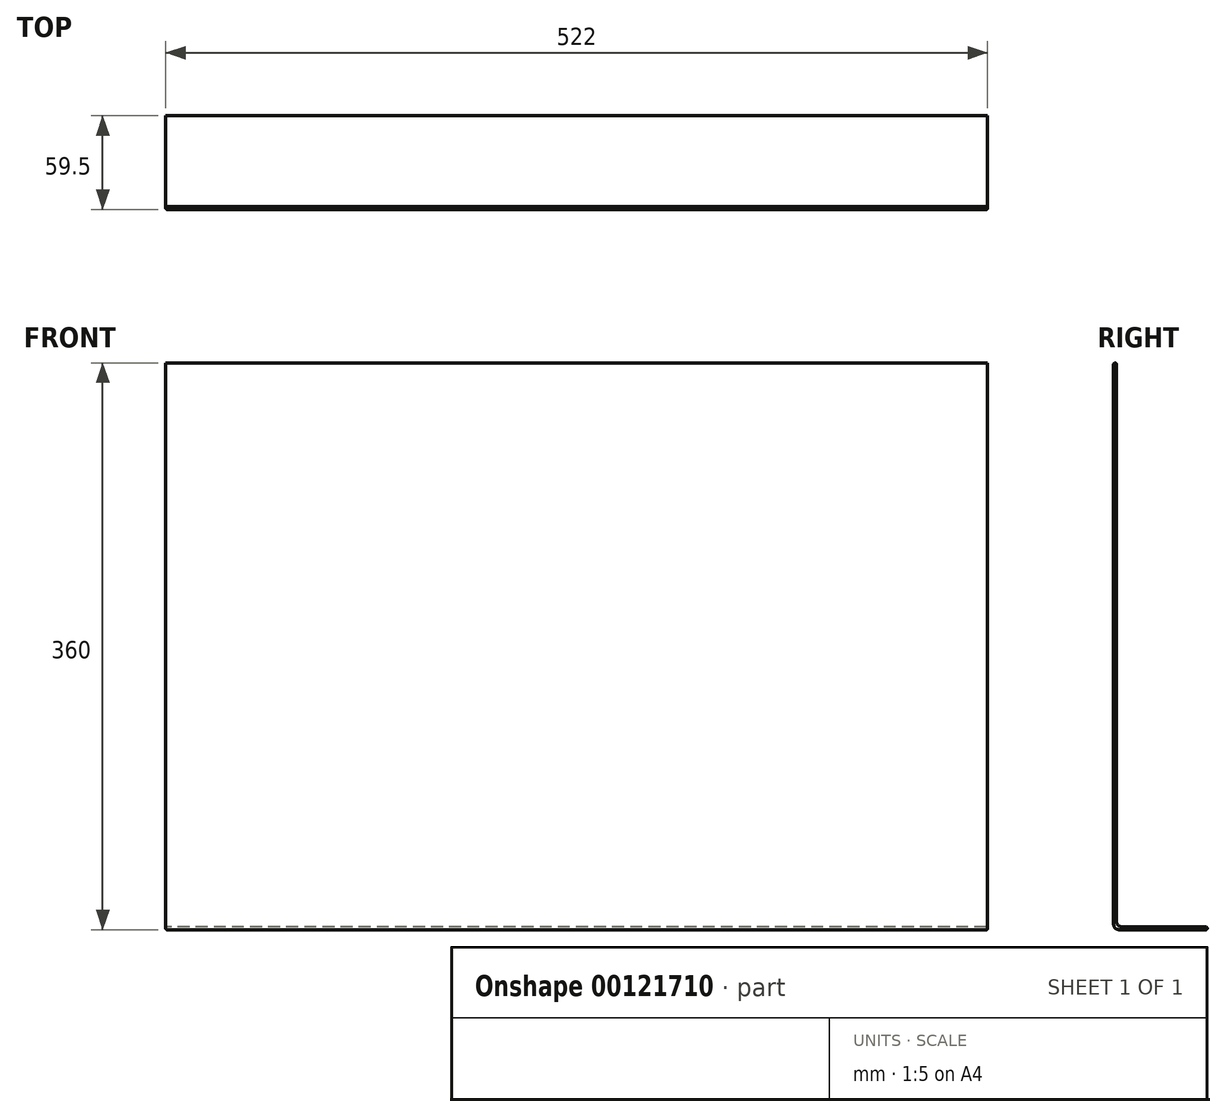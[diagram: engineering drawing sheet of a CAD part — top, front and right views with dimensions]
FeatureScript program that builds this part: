
annotation { "Feature Type Name" : "Feature", "Feature Type Description" : "" }
export const myFeature = defineFeature(function(context is Context, id is Id, definition is map)
    precondition{}
    {
        {
            assignVariable(context, id + "F0", {"name" : "thick", "anyValue" : 1.8});
        }
        {
            var Q0;
            Q0=qCreatedBy(makeId("Right.planeOp"),FACE);
            var sketch = newSketch(context, id + "F1", { "sketchPlane" : qUnion([Q0])});
            skLineSegment(sketch, "E0", {"start": v(0, 0) * mm, "end": v(0, 360) * mm});
            skLineSegment(sketch, "E1", {"start": v(0, 360) * mm, "end": v(1.8, 360) * mm});
            skLineSegment(sketch, "E2", {"start": v(1.8, 360) * mm, "end": v(1.8, 1.8) * mm});
            skLineSegment(sketch, "E3", {"start": v(1.8, 1.8) * mm, "end": v(59.5, 1.8) * mm});
            skLineSegment(sketch, "E4", {"start": v(59.5, 1.8) * mm, "end": v(59.5, 0) * mm});
            skLineSegment(sketch, "E5", {"start": v(59.5, 0) * mm, "end": v(0, 0) * mm});
            skSolve(sketch);
        }
        {
            var Q0;
            Q0=makeQuery(id+"F1.imprint","IMPRINT",FACE,{"disambiguationData":[TD([[makeQuery(id+"F1.imprint","IMPRINT",EDGE,{"derivedFrom":sQuery(id+"F1.wireOp",EDGE,"E0")}),-1.0]])]});
            extrude(context, id + "F2", {"entities" : qUnion([Q0]), "depth" : (522 / 2) * mm});
        }
        {
            var Q0;
            Q0=makeQuery(id+"F2.opExtrude","SWEPT_EDGE",EDGE,{"disambiguationData":[OSD([sQuery(id+"F1.wireOp",EDGE,"E2"),sQuery(id+"F1.wireOp",EDGE,"E3")])]});
            var Q1;
            Q1=makeQuery(id+"F2.opExtrude","SWEPT_EDGE",EDGE,{"disambiguationData":[OSD([sQuery(id+"F1.wireOp",EDGE,"E0"),sQuery(id+"F1.wireOp",EDGE,"E5")])]});
            fillet(context, id + "F3", {"entities" : qUnion([Q0, Q1]), "radius" : 2 * (getVariable(context, 'thick')) * mm, "tangentPropagation" : true, "allowEdgeOverflow" : false});
        }
        {
            var Q0;
            Q0=makeQuery(id+"F2.opExtrude","CAP_EDGE",EDGE,{"disambiguationData":[OSD([sQuery(id+"F1.wireOp",EDGE,"E3")])],"isStart":false});
            var Q1;
            Q1=makeQuery(id+"F2.opExtrude","CAP_EDGE",EDGE,{"disambiguationData":[OSD([sQuery(id+"F1.wireOp",EDGE,"E5")])],"isStart":false});
            var Q2;
            Q2=makeQuery(id+"F2.opExtrude","SWEPT_EDGE",EDGE,{"disambiguationData":[OSD([sQuery(id+"F1.wireOp",EDGE,"E3"),sQuery(id+"F1.wireOp",EDGE,"E4")])]});
            var Q3;
            Q3=makeQuery(id+"F2.opExtrude","SWEPT_EDGE",EDGE,{"disambiguationData":[OSD([sQuery(id+"F1.wireOp",EDGE,"E4"),sQuery(id+"F1.wireOp",EDGE,"E5")])]});
            var Q4;
            Q4=makeQuery(id+"F2.opExtrude","CAP_EDGE",EDGE,{"disambiguationData":[OSD([sQuery(id+"F1.wireOp",EDGE,"E2")])],"isStart":false});
            var Q5;
            Q5=makeQuery(id+"F2.opExtrude","CAP_EDGE",EDGE,{"disambiguationData":[OSD([sQuery(id+"F1.wireOp",EDGE,"E0")])],"isStart":false});
            var Q6;
            Q6=makeQuery(id+"F2.opExtrude","SWEPT_EDGE",EDGE,{"disambiguationData":[OSD([sQuery(id+"F1.wireOp",EDGE,"E0"),sQuery(id+"F1.wireOp",EDGE,"E1")])]});
            var Q7;
            Q7=makeQuery(id+"F2.opExtrude","SWEPT_EDGE",EDGE,{"disambiguationData":[OSD([sQuery(id+"F1.wireOp",EDGE,"E1"),sQuery(id+"F1.wireOp",EDGE,"E2")])]});
            var Q8;
            {var subQ0=sQuery(id+"F1.wireOp",EDGE,"E3");var subQ1=sQuery(id+"F1.wireOp",EDGE,"E2");Q8=makeQuery(id+"F3.opFillet","BLEND_EDGE",EDGE,{"blendedFrom":[makeQuery(id+"F2.opExtrude","SWEPT_EDGE",EDGE,{"disambiguationData":[OSD([subQ1,subQ0])]}),makeQuery(id+"F2.opExtrude","CAP_FACE",FACE,{"disambiguationData":[OSD([sQuery(id+"F1.wireOp",EDGE,"E0"),sQuery(id+"F1.wireOp",EDGE,"E1"),subQ1,subQ0,sQuery(id+"F1.wireOp",EDGE,"E4"),sQuery(id+"F1.wireOp",EDGE,"E5")])],"isStart":false})],"blendedInto":[makeQuery(id+"F2.opExtrude","CAP_FACE",FACE,{"disambiguationData":[OSD([sQuery(id+"F1.wireOp",EDGE,"E0"),sQuery(id+"F1.wireOp",EDGE,"E1"),subQ1,subQ0,sQuery(id+"F1.wireOp",EDGE,"E4"),sQuery(id+"F1.wireOp",EDGE,"E5")])],"isStart":false})]});}
            var Q9;
            {var subQ0=sQuery(id+"F1.wireOp",EDGE,"E5");var subQ1=sQuery(id+"F1.wireOp",EDGE,"E0");Q9=makeQuery(id+"F3.opFillet","BLEND_EDGE",EDGE,{"blendedFrom":[makeQuery(id+"F2.opExtrude","SWEPT_EDGE",EDGE,{"disambiguationData":[OSD([subQ1,subQ0])]}),makeQuery(id+"F2.opExtrude","CAP_FACE",FACE,{"disambiguationData":[OSD([subQ1,sQuery(id+"F1.wireOp",EDGE,"E1"),sQuery(id+"F1.wireOp",EDGE,"E2"),sQuery(id+"F1.wireOp",EDGE,"E3"),sQuery(id+"F1.wireOp",EDGE,"E4"),subQ0])],"isStart":false})],"blendedInto":[makeQuery(id+"F2.opExtrude","CAP_FACE",FACE,{"disambiguationData":[OSD([subQ1,sQuery(id+"F1.wireOp",EDGE,"E1"),sQuery(id+"F1.wireOp",EDGE,"E2"),sQuery(id+"F1.wireOp",EDGE,"E3"),sQuery(id+"F1.wireOp",EDGE,"E4"),subQ0])],"isStart":false})]});}
            fillet(context, id + "F4", {"entities" : qUnion([Q0, Q1, Q2, Q3, Q4, Q5, Q6, Q7, Q8, Q9]), "radius" : (getVariable(context, 'thick') / 2) * mm, "allowEdgeOverflow" : false});
        }
        {
            var Q0;
            Q0=makeQuery(id+"F2.opExtrude","SWEPT_BODY",BODY,{"disambiguationData":[OSD([sQuery(id+"F1.wireOp",EDGE,"E0"),sQuery(id+"F1.wireOp",EDGE,"E1"),sQuery(id+"F1.wireOp",EDGE,"E2"),sQuery(id+"F1.wireOp",EDGE,"E3"),sQuery(id+"F1.wireOp",EDGE,"E4"),sQuery(id+"F1.wireOp",EDGE,"E5")])]});
            var Q1;
            Q1=makeQuery(id+"F2.opExtrude","CAP_FACE",FACE,{"disambiguationData":[OSD([sQuery(id+"F1.wireOp",EDGE,"E0"),sQuery(id+"F1.wireOp",EDGE,"E1"),sQuery(id+"F1.wireOp",EDGE,"E2"),sQuery(id+"F1.wireOp",EDGE,"E3"),sQuery(id+"F1.wireOp",EDGE,"E4"),sQuery(id+"F1.wireOp",EDGE,"E5")])],"isStart":true});
            mirror(context, id + "F5", {"operationType" : NewBodyOperationType.ADD, "entities" : qUnion([Q0]), "mirrorPlane" : qUnion([Q1])});
        }
    });
